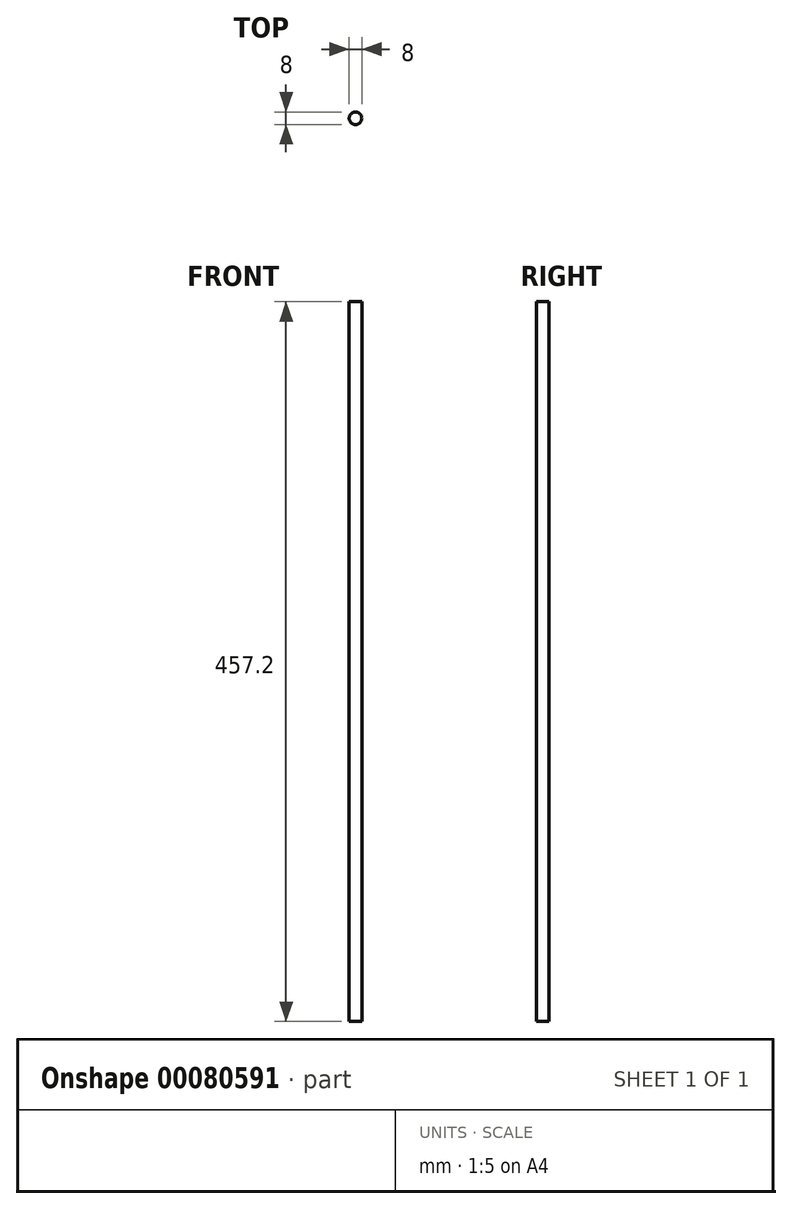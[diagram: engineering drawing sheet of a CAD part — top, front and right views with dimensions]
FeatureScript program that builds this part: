
annotation { "Feature Type Name" : "Feature", "Feature Type Description" : "" }
export const myFeature = defineFeature(function(context is Context, id is Id, definition is map)
    precondition{}
    {
        {
            var Q0;
            Q0=qCreatedBy(makeId("Top.planeOp"),FACE);
            var sketch = newSketch(context, id + "F0", { "sketchPlane" : qUnion([Q0])});
            skCircle(sketch, "E0", {"center": v(0, 0) * mm, "radius": 4 * mm});
            skSolve(sketch);
        }
        {
            var Q0;
            Q0=qSketchRegion(id+"F0",true);
            extrude(context, id + "F1", {"entities" : qUnion([Q0]), "depth" : 457.2 * mm});
        }
    });
